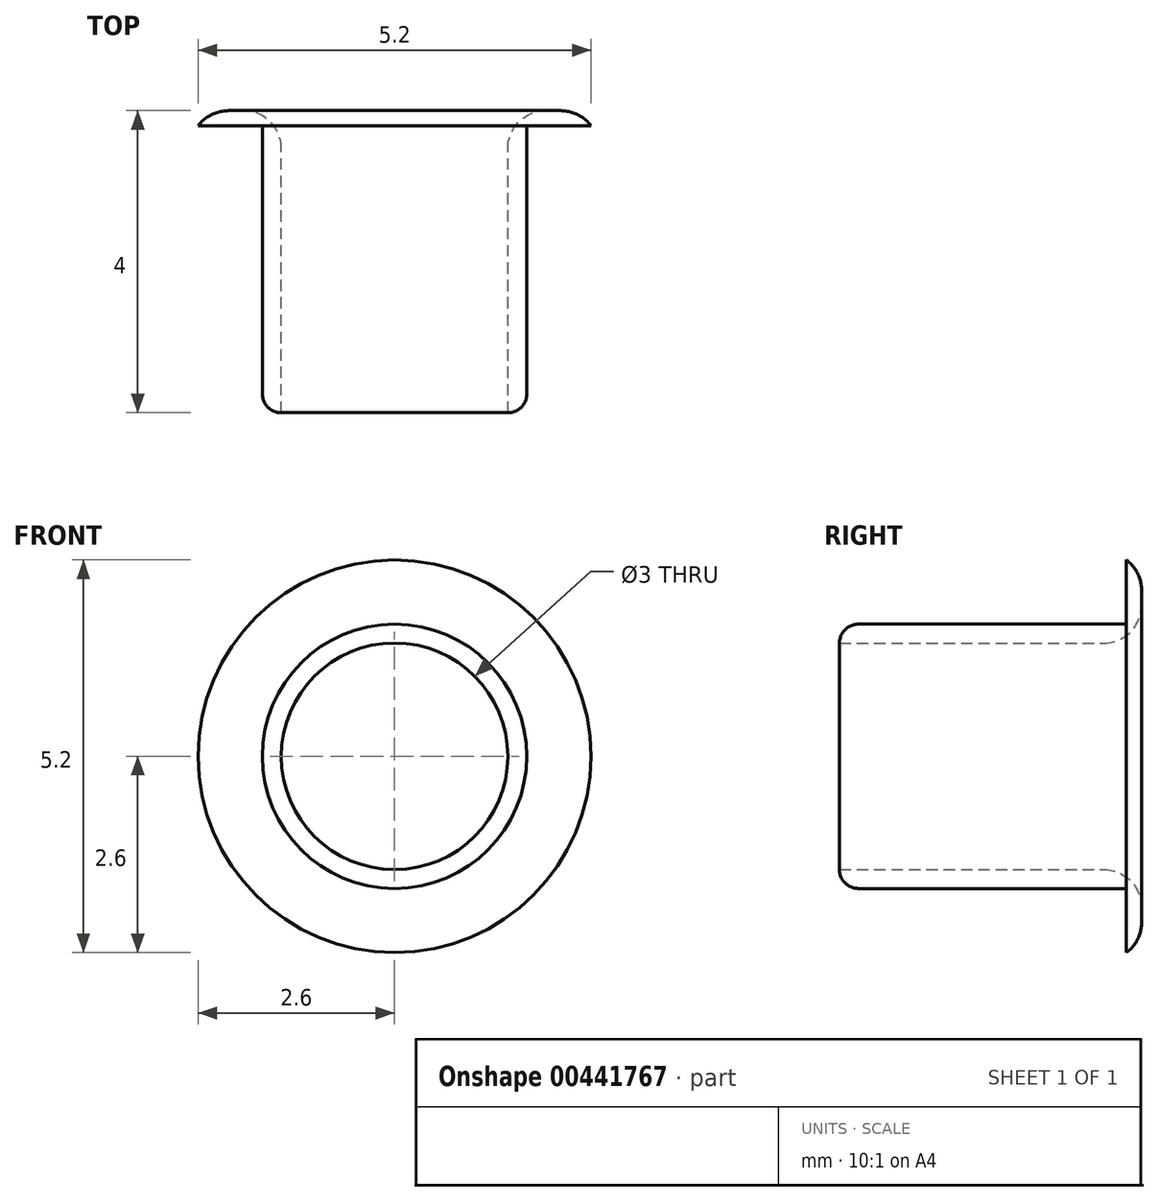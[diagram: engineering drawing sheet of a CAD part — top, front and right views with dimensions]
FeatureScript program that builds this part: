
annotation { "Feature Type Name" : "Feature", "Feature Type Description" : "" }
export const myFeature = defineFeature(function(context is Context, id is Id, definition is map)
    precondition{}
    {
        {
            var Q0;
            Q0=qCreatedBy(makeId("Front.planeOp"),FACE);
            var sketch = newSketch(context, id + "F0", { "sketchPlane" : qUnion([Q0])});
            skCircle(sketch, "E0", {"center": v(0, 0) * mm, "radius": 1.5 * mm});
            skCircle(sketch, "E1", {"center": v(0, 0) * mm, "radius": 1.75 * mm});
            skSolve(sketch);
        }
        {
            var Q0;
            Q0 = qSketchRegion(id + "F0", true);
            extrude(context, id + "F1", {"entities" : qUnion([Q0]), "depth" : 4 * mm});
        }
        {
            var Q0;
            Q0=qCreatedBy(makeId("Front.planeOp"),FACE);
            var sketch = newSketch(context, id + "F2", { "sketchPlane" : qUnion([Q0])});
            skCircle(sketch, "E2", {"center": v(0, 0) * mm, "radius": 2.6 * mm});
            skCircle(sketch, "E3", {"center": v(0, 0) * mm, "radius": 1.75 * mm});
            skSolve(sketch);
        }
        {
            var Q0;
            Q0 = qSketchRegion(id + "F2", true);
            extrude(context, id + "F3", {"entities" : qUnion([Q0]), "operationType" : NewBodyOperationType.ADD, "depth" : 0.2 * mm});
        }
        {
            var Q0;
            Q0=makeQuery(id+"F1.opExtrude","CAP_EDGE",EDGE,{"disambiguationData":[OSD([sQuery(id+"F0.wireOp",EDGE,"E1")])],"isStart":false});
            fillet(context, id + "F4", {"entities" : qUnion([Q0]), "radius" : 0.25 * mm, "tangentPropagation" : true, "allowEdgeOverflow" : false});
        }
        {
            var Q0;
            Q0=makeQuery(id+"F3.opExtrude","CAP_EDGE",EDGE,{"disambiguationData":[OSD([sQuery(id+"F2.wireOp",EDGE,"E2")])],"isStart":true});
            var Q1;
            Q1=makeQuery(id+"F1.opExtrude","CAP_EDGE",EDGE,{"disambiguationData":[OSD([sQuery(id+"F0.wireOp",EDGE,"E0")])],"isStart":true});
            fillet(context, id + "F5", {"entities" : qUnion([Q0, Q1]), "radius" : 0.5 * mm, "tangentPropagation" : true, "allowEdgeOverflow" : false});
        }
    });
